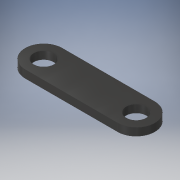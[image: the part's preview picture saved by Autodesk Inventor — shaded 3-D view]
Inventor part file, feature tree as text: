
AUTODESK INVENTOR PART (.ipt)
format: ipt  version: 2017 (Build 210142000, 142)  size: 116,224 bytes
history: native  units: in
note: dims shown in document units (in); Inventor stores cm internally (conversion verified against a paired STEP export)
features: extrude x1, sketch x1
ambient origin geometry x8: Origin, YZ Plane, XZ Plane, XY Plane, X Axis, Y Axis, Z Axis, Center Point
bodies: Body1 (feature_tree)
feature tree (2):
  extrude  "Extrusion2"  Depth=0.9449in
  sketch  "Sketch1"  dims[d0=2.3622in d1=0.9449in d2=0.5118in d5=0.1969in d6=0.1969in d8=0.1969in d9=0.0in d10=0.1575in]
